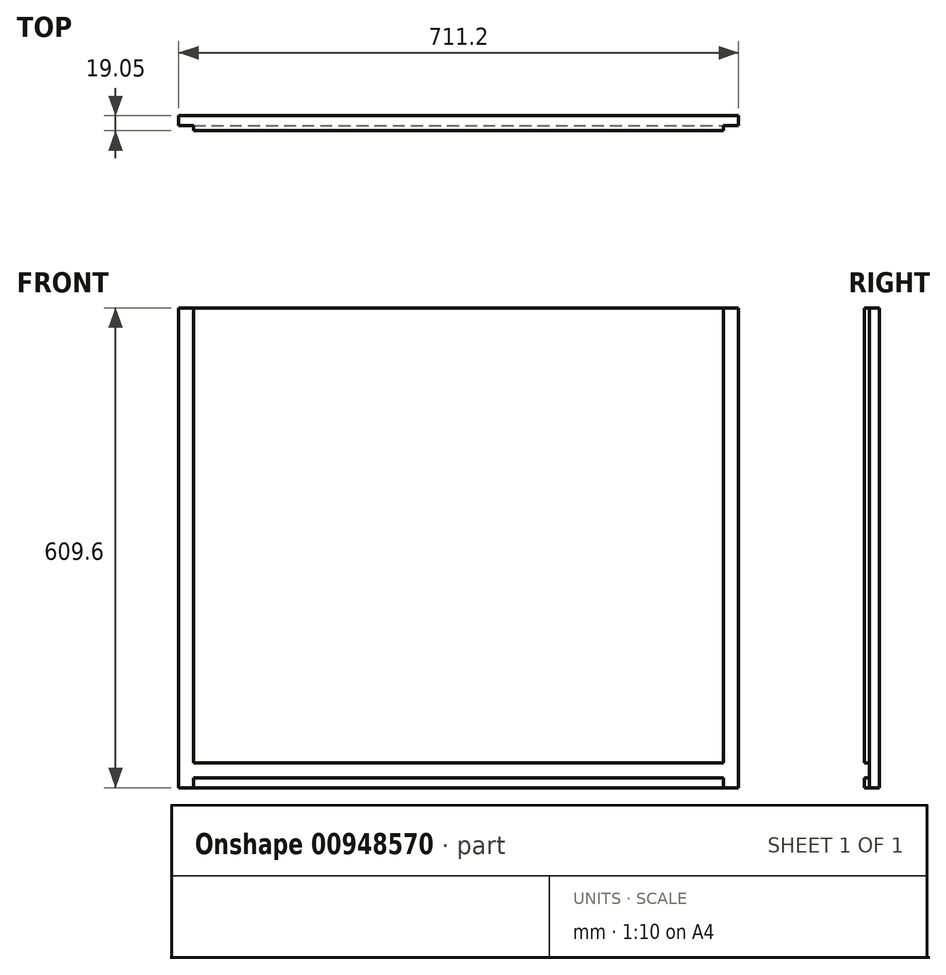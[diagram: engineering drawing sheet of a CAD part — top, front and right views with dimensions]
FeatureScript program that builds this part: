
annotation { "Feature Type Name" : "Feature", "Feature Type Description" : "" }
export const myFeature = defineFeature(function(context is Context, id is Id, definition is map)
    precondition{}
    {
        {
            var Q0;
            Q0=qCreatedBy(makeId("Front.planeOp"),FACE);
            var sketch = newSketch(context, id + "F0", { "sketchPlane" : qUnion([Q0])});
            skLineSegment(sketch, "E0.bottom", {"start": v(355.6, -304.8) * mm, "end": v(-355.6, -304.8) * mm});
            skLineSegment(sketch, "E0.top", {"start": v(355.6, 304.8) * mm, "end": v(-355.6, 304.8) * mm});
            skLineSegment(sketch, "E0.left", {"start": v(355.6, -304.8) * mm, "end": v(355.6, 304.8) * mm});
            skLineSegment(sketch, "E0.right", {"start": v(-355.6, -304.8) * mm, "end": v(-355.6, 304.8) * mm});
            skPoint(sketch, "E0.middle", {"position": v(0, 0) * mm});
            skSolve(sketch);
        }
        {
            var Q0;
            Q0=makeQuery(id+"F0.imprint","IMPRINT",FACE,{"disambiguationData":[TD([[makeQuery(id+"F0.imprint","IMPRINT",EDGE,{"derivedFrom":sQuery(id+"F0.wireOp",EDGE,"E0.bottom")}),-1.0]])]});
            extrude(context, id + "F1", {"entities" : qUnion([Q0]), "depth" : 19.05 * mm, "offsetDistance" : 25.4 * mm});
        }
        {
            var Q0;
            Q0=makeQuery(id+"F1.opExtrude","CAP_FACE",FACE,{"disambiguationData":[OSD([sQuery(id+"F0.wireOp",EDGE,"E0.bottom"),sQuery(id+"F0.wireOp",EDGE,"E0.top"),sQuery(id+"F0.wireOp",EDGE,"E0.left"),sQuery(id+"F0.wireOp",EDGE,"E0.right")])],"isStart":false});
            var sketch = newSketch(context, id + "F2", { "sketchPlane" : qUnion([Q0])});
            skLineSegment(sketch, "E1.bottom", {"start": v(-355.6, -273.05) * mm, "end": v(355.6, -273.05) * mm});
            skLineSegment(sketch, "E1.top", {"start": v(-355.6, -292.1) * mm, "end": v(355.6, -292.1) * mm});
            skLineSegment(sketch, "E1.left", {"start": v(-355.6, -273.05) * mm, "end": v(-355.6, -292.1) * mm});
            skLineSegment(sketch, "E1.right", {"start": v(355.6, -273.05) * mm, "end": v(355.6, -292.1) * mm});
            skLineSegment(sketch, "E2.bottom", {"start": v(-336.55, 304.8) * mm, "end": v(-355.6, 304.8) * mm});
            skLineSegment(sketch, "E2.top", {"start": v(-336.55, -304.8) * mm, "end": v(-355.6, -304.8) * mm});
            skLineSegment(sketch, "E2.left", {"start": v(-336.55, 304.8) * mm, "end": v(-336.55, -304.8) * mm});
            skLineSegment(sketch, "E2.right", {"start": v(-355.6, 304.8) * mm, "end": v(-355.6, -304.8) * mm});
            skLineSegment(sketch, "E3.bottom", {"start": v(336.55, 304.8) * mm, "end": v(355.6, 304.8) * mm});
            skLineSegment(sketch, "E3.top", {"start": v(336.55, -304.8) * mm, "end": v(355.6, -304.8) * mm});
            skLineSegment(sketch, "E3.left", {"start": v(336.55, 304.8) * mm, "end": v(336.55, -304.8) * mm});
            skLineSegment(sketch, "E3.right", {"start": v(355.6, 304.8) * mm, "end": v(355.6, -304.8) * mm});
            skSolve(sketch);
        }
        {
            var Q0;
            {var subQ5=sQuery(id+"F2.wireOp",EDGE,"E2.bottom");Q0=makeQuery(id+"F2.imprint","IMPRINT",FACE,{"disambiguationData":[TD([[makeQuery(id+"F2.imprint","IMPRINT",EDGE,{"derivedFrom":subQ5}),1.0]])]});}
            var Q1;
            {var subQ0=sQuery(id+"F2.wireOp",EDGE,"E2.right");var subQ1=sQuery(id+"F2.wireOp",EDGE,"E1.bottom");var subQ2=makeQuery(id+"F2.imprint","INTERSECT",VERTEX,{"derivedFrom":[subQ1,subQ0]});Q1=makeQuery(id+"F2.imprint","IMPRINT",FACE,{"disambiguationData":[TD([[makeQuery(id+"F2.imprint","IMPRINT",EDGE,{"disambiguationData":[TD([[subQ2,-1.0]])],"derivedFrom":subQ1}),-1.0]])]});}
            var Q2;
            {var subQ5=sQuery(id+"F2.wireOp",EDGE,"E2.top");Q2=makeQuery(id+"F2.imprint","IMPRINT",FACE,{"disambiguationData":[TD([[makeQuery(id+"F2.imprint","IMPRINT",EDGE,{"derivedFrom":subQ5}),-1.0]])]});}
            var Q3;
            {var subQ0=sQuery(id+"F2.wireOp",EDGE,"E2.left");var subQ1=sQuery(id+"F2.wireOp",EDGE,"E1.bottom");var subQ2=makeQuery(id+"F2.imprint","INTERSECT",VERTEX,{"derivedFrom":[subQ1,subQ0]});Q3=makeQuery(id+"F2.imprint","IMPRINT",FACE,{"disambiguationData":[TD([[makeQuery(id+"F2.imprint","IMPRINT",EDGE,{"disambiguationData":[TD([[subQ2,-1.0]])],"derivedFrom":subQ1}),-1.0]])]});}
            var Q4;
            {var subQ0=sQuery(id+"F2.wireOp",EDGE,"E3.right");var subQ1=sQuery(id+"F2.wireOp",EDGE,"E1.bottom");var subQ2=makeQuery(id+"F2.imprint","INTERSECT",VERTEX,{"derivedFrom":[subQ1,subQ0]});Q4=makeQuery(id+"F2.imprint","IMPRINT",FACE,{"disambiguationData":[TD([[makeQuery(id+"F2.imprint","IMPRINT",EDGE,{"disambiguationData":[TD([[subQ2,1.0]])],"derivedFrom":subQ1}),-1.0]])]});}
            var Q5;
            {var subQ5=sQuery(id+"F2.wireOp",EDGE,"E3.bottom");Q5=makeQuery(id+"F2.imprint","IMPRINT",FACE,{"disambiguationData":[TD([[makeQuery(id+"F2.imprint","IMPRINT",EDGE,{"derivedFrom":subQ5}),1.0]])]});}
            var Q6;
            {var subQ5=sQuery(id+"F2.wireOp",EDGE,"E3.top");Q6=makeQuery(id+"F2.imprint","IMPRINT",FACE,{"disambiguationData":[TD([[makeQuery(id+"F2.imprint","IMPRINT",EDGE,{"derivedFrom":subQ5}),-1.0]])]});}
            extrude(context, id + "F3", {"entities" : qUnion([Q0, Q1, Q2, Q3, Q4, Q5, Q6]), "operationType" : NewBodyOperationType.REMOVE, "oppositeDirection" : true, "depth" : 6.35 * mm, "offsetDistance" : 25.4 * mm});
        }
    });
